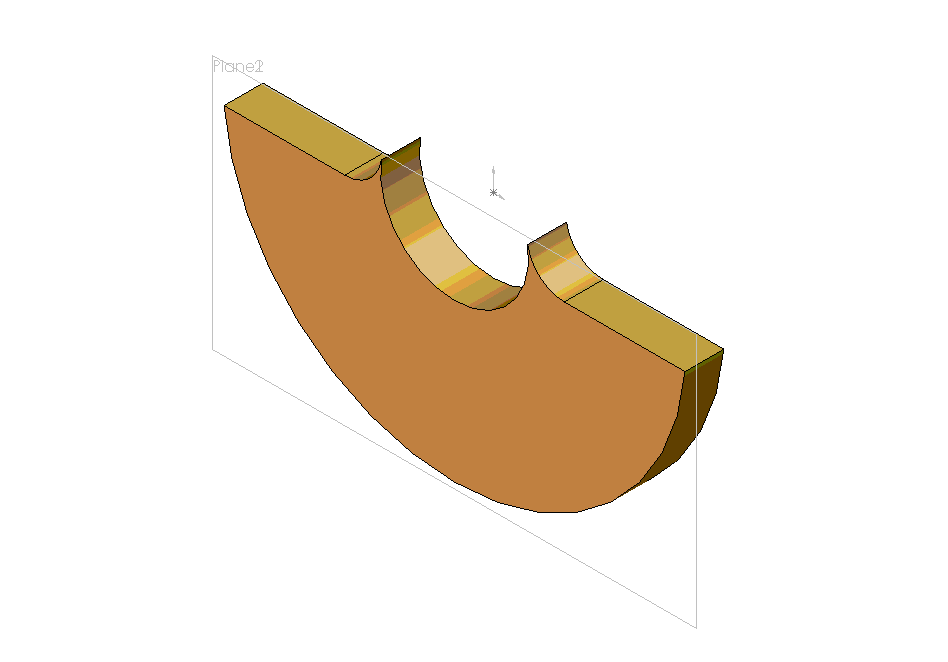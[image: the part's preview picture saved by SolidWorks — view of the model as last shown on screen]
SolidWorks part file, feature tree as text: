
SOLIDWORKS PART (.sldprt)
format: sldprt  version: not decoded by parser v0  size: 115,712 bytes
history: native  units: mm
features: sketch x3, extrude x2, plane x2, material x1, cut_extrude x1 (+12 scaffold rows collapsed)
feature tree (21):
  scaffold x12  (default folders/planes/origin — collapsed)
  material  "Material <not specified>"
  sketch  "Sketch1"  dims[D1=50.0mm D2=16.0mm]
  extrude  "Base-Extrude"  Depth=4.2mm
  plane  "Plane1"  Offset=0mm
  sketch  "Sketch2"  dims[D1=2.2mm]
  cut_extrude  "Cut-Extrude1"  [1 undecoded]
  plane  "Plane2"  Offset=0mm
  sketch  "Sketch3"  dims[D1=16.0mm D3=8.0mm D4=8.0mm D2=2.2mm]
  extrude  "Boss-Extrude1"  Depth=4.2mm
decode coverage: 5 of 6 modeling features carry decoded parameters
note: 1 parameter value undecoded
note: suppression state not decoded; provenance and decode notes live in map.json
